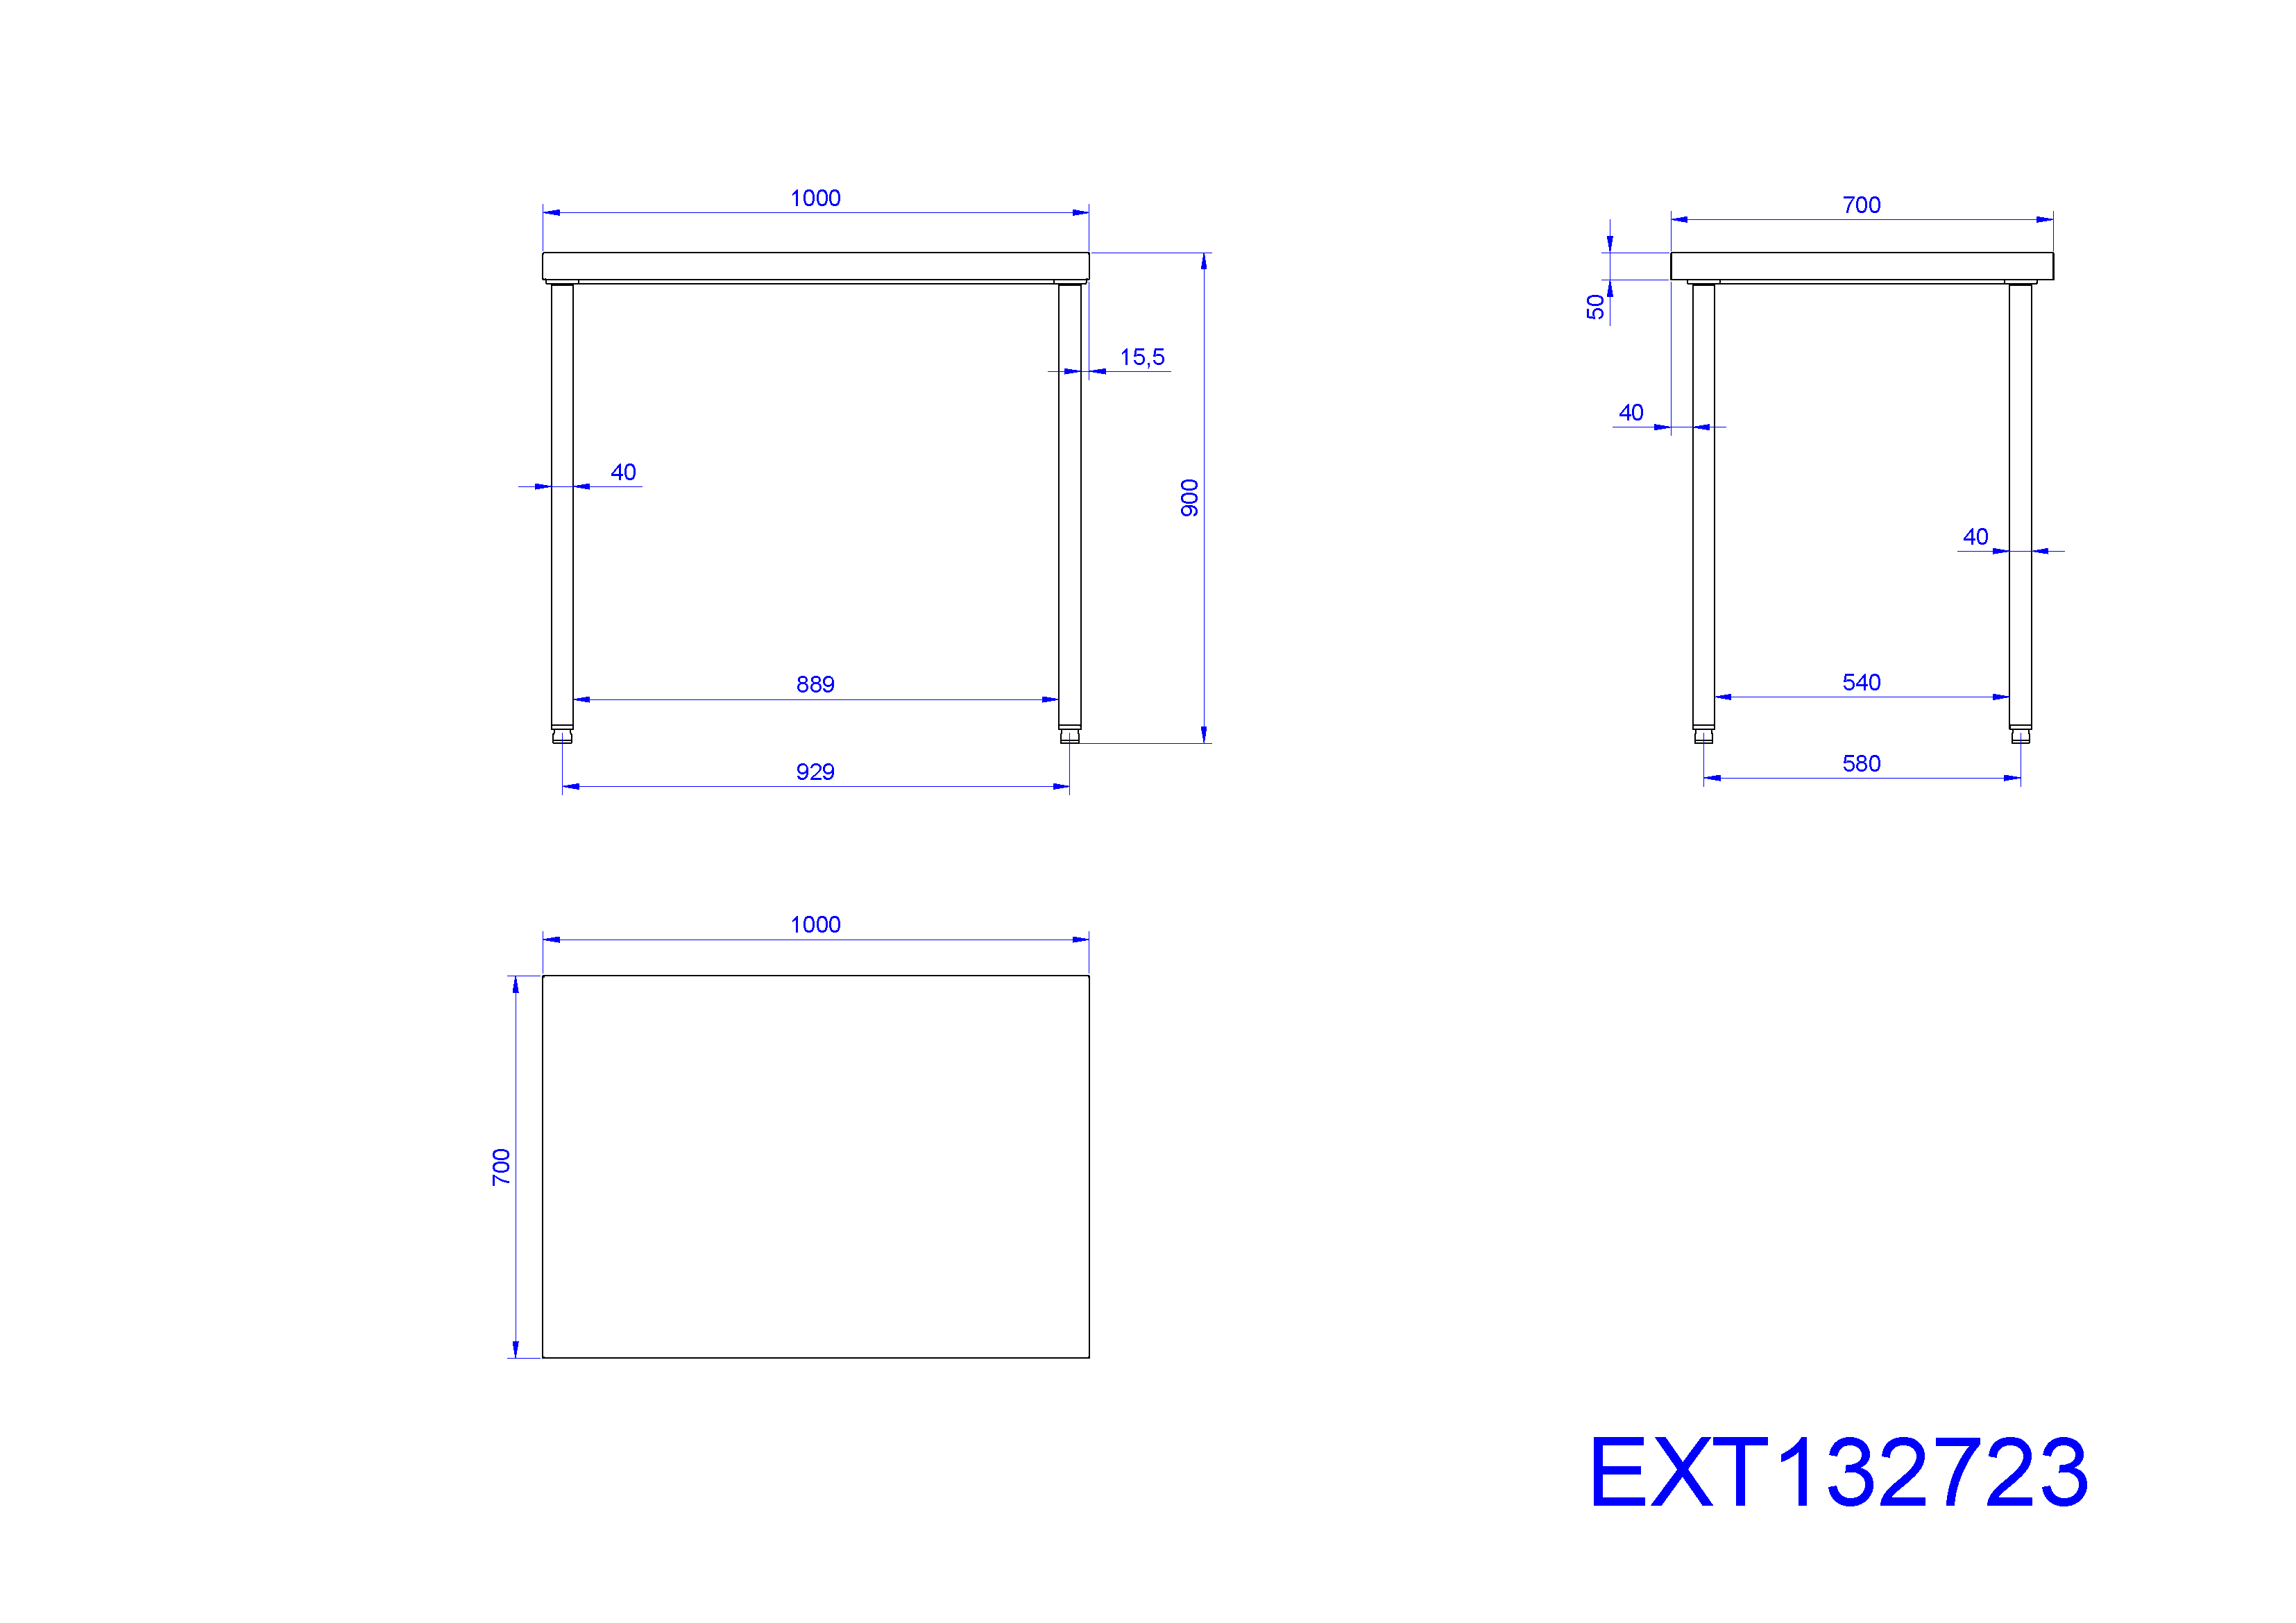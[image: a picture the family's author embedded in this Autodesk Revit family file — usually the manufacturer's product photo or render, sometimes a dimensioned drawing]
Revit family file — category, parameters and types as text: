
# Revit family: QF_ELECTROLUXPROFESSIONAL_134133_GLG1216DXP
name_source: partatom
category: Attrezzature speciali
units: mm (PartAtom-declared; Revit-internal decimal feet)

## family parameters
Basato su piano di lavoro = No
Condiviso = No
Punto di calcolo locali = No
Quota connettore circolare = Usa diametro
Sempre verticale = Sì
Taglio con vuoti quando caricato = No
Tipo di parte = Normale

## types (1)
- Standard
    Accessory = Sì
    Cold Water Size = 0 mm
    Compressed Air Pressure = 0.0 Pa
    Compressed Air Size = 0 mm
    Compressed Air Volume = 0.0 L/s
    Condensate Return Size = 0 mm
    Cycle = 0 Hz
    Depth Actual = 700 mm  [stored 2.29659 ft]
    Descrizione = SINK CUPBOARD 1 BOWL+ R/H DRAINER 1200MM
    Direct Waste Size = 0 mm
    Gas Input Pressure = 0
    Gas KW = 0
    Gas Size = 0 mm
    HP = 0 HP
    Height Actual = 1000 mm  [stored 3.28084 ft]
    Hot Water Size = 0 mm
    Item Number = 134133
    Length Actual = 1200 mm  [stored 3.93701 ft]
    Modello = GLG1216DXP
    Phase = 0
    Produttore = Electrolux Professional
    Prospetto di default = 0 mm  [stored 0 ft]
    Refrigerant Compressor Remote = Sì
    Refrigeration Liquid Line Size = 0 mm  [stored 0 ft]
    Refrigeration Suction Line Size = 0 mm  [stored 0 ft]
    Steam Consumption per Hour = 0
    Steam Supply Maximum Pressure = 0.0 Pa
    Steam Supply Minimum Pressure = 0.0 Pa
    Steam Supply Size = 0 mm
    URL = https://www.electroluxprofessional.com
    URL Manufacturer = https://www.electroluxprofessional.com
    Volts = 0 V
    Watts = 0 W
    Weight = 47.00 kg

note: source unit labels omitted for Gas Input Pressure — the stored unit's dimension contradicts the parameter name (converter mislabeling)

note: [stored X ft] marks values corroborated as IEEE doubles in the binary element streams (Revit-internal decimal feet)

## geometry (parser evidence)
native form markers: Blend x4, Sweep x4
no freeform markers — native parametric forms only
